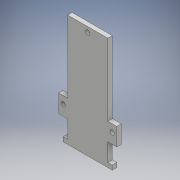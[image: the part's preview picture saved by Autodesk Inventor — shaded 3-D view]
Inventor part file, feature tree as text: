
AUTODESK INVENTOR PART (.ipt)
format: ipt  version: 2017 (Build 210142000, 142)  size: 138,240 bytes
history: native  units: mm
features: extrude x2, sketch x2
ambient origin geometry x8: Origin, YZ Plane, XZ Plane, XY Plane, X Axis, Y Axis, Z Axis, Center Point
bodies: Solid1 (feature_tree)
feature tree (4):
  extrude  "Extrusion1"  Depth=3.0mm
  extrude  "Extrusion2"  Depth=33.0mm
  sketch  "Sketch1"  dims[d2=3.0mm d3=0.0mm d8=3.0mm]
  sketch  "Sketch5"  dims[d9=3.0mm d11=33.0mm d12=12.0mm d13=60.415173mm d14=12.0mm d24=6.0mm d25=6.0mm d36=5.0mm d37=3.0mm d38=5.0mm d39=3.0mm d41=13.5mm d42=3.0mm d43=0.0mm d44=0.0mm d46=72.0mm]
